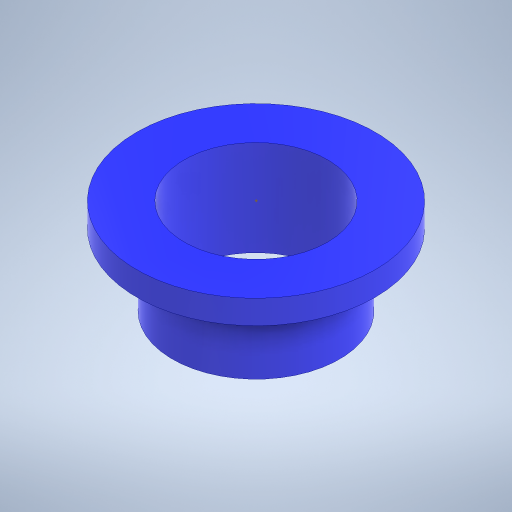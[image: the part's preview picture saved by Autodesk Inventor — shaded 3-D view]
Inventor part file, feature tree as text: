
AUTODESK INVENTOR PART (.ipt)
format: ipt  version: 2024 (Build 280153000, 153)  size: 248,832 bytes
history: native  units: mm
features: extrude x2, sketch x2
ambient origin geometry x8: Origin, YZ Plane, XZ Plane, XY Plane, X Axis, Y Axis, Z Axis, Center Point
bodies: Solid1 (feature_tree)
feature tree (4):
  extrude  "Extrusion1"  Depth=7.0mm
  extrude  "Extrusion2"  Depth=1.0mm
  sketch  "Sketch3"  dims[d2=3.0mm d3=0.0mm d4=13.0mm d5=1.0mm d6=0.0mm]
  sketch  "Sketch2"  dims[d0=6.0mm d1=7.0mm]
